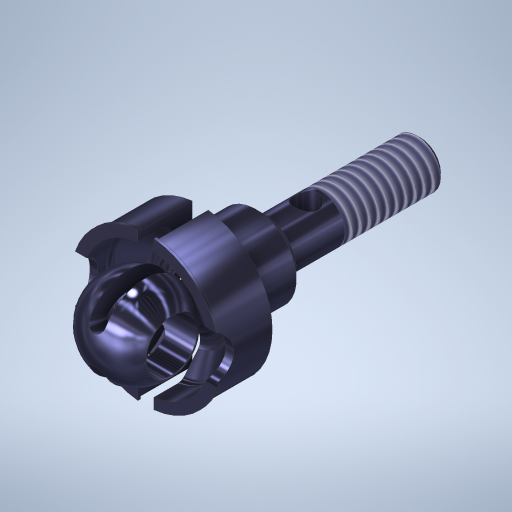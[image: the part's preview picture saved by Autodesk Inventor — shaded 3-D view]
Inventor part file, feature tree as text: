
AUTODESK INVENTOR PART (.ipt)
format: ipt  version: 2023.1 (Build 271208000, 208)  size: 541,184 bytes
history: native  units: in
note: dims shown in document units (in); Inventor stores cm internally (conversion verified against a paired STEP export)
features: sketch x7, extrude x5, chamfer x3, projected_geometry x3, revolve x2, fillet x2, plane x1, mirror x1, thread x1, other x1
ambient origin geometry x8: Origin, YZ Plane, XZ Plane, XY Plane, X Axis, Y Axis, Z Axis, Center Point
bodies: Solid1 (feature_tree)
feature tree (26):
  extrude  "Extrusion1"  Depth=0.86in TaperAngle=0.0deg
  extrude  "Extrusion2"  Depth=0.15in
  chamfer  "Chamfer1"  Distance=0.015in Angle=45.0deg
  revolve  "Revolution1"  [1 undecoded]
  fillet  "Fillet1"  Radius=0.01in
  fillet  "Fillet2"  Radius=0.2125in
  extrude  "Extrusion3"  Depth=0.032in
  chamfer  "Chamfer2"  Angle=90.0deg  [1 undecoded]
  plane  "Work Plane1"
  revolve  "Revolution2"  [1 undecoded]
  mirror  "Mirror1"
  extrude  "Extrusion4"  Depth=0.25in
  chamfer  "Chamfer3"  Distance=0.315in
  extrude  "Extrusion5"  Depth=0.25in TaperAngle=0.0deg
  thread  "Thread1"  [1 undecoded]
  sketch  "Sketch1"  dims[d0=0.1875in d1=0.86in d2=0.0in]
  sketch  "Sketch2"  dims[d3=0.3in d4=0.15in d5=-0.2749in d6=0.015in d7=0.125in d8=45.0deg]
  sketch  "Sketch3"  dims[d9=0.5625in d11=0.01in d12=0.01in d13=0.2125in]
  sketch  "Sketch4"  dims[d14=0.032in d15=0.032in]
  other  "Work Point1"
  sketch  "Sketch5"  dims[d16=0.1in]
  sketch  "Sketch6"  dims[d17=0.1in]
  sketch  "Sketch7"  dims[d18=0.35in d19=90.0deg d20=0.02in d21=0.032in d22=0.315in d23=0.25in d24=0.0in d25=0.032in d26=0.125in d27=45.0deg d28=0.0312in d29=0.5in d30=0.56in d31=90.0deg d32=0.2in d33=0.25in d34=0.0in d35=0.005in d36=0.125in d37=45.0deg d38=0.094in d39=0.448in d40=0.25in d41=0.0in d42=0.375in d43=0.0in]
  projected_geometry  "Project Cut Edges1"
  projected_geometry  "Project Cut Edges2"
  projected_geometry  "Project Cut Edges3"
note: 4 required parameter values undecoded (feature->parameter linkage not recoverable at this tier; creation-order binding heuristic only, values carry confidence <= 0.55)